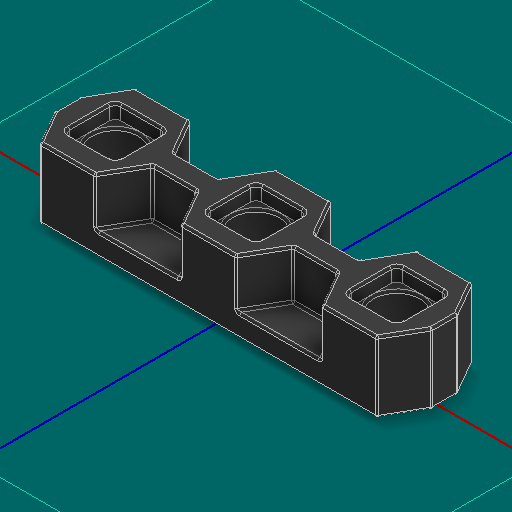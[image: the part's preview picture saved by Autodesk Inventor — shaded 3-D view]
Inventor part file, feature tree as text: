
AUTODESK INVENTOR PART (.ipt)
format: ipt  version: 2025 (Build 290162000, 162)  size: 506,880 bytes
history: native  units: in
note: dims shown in document units (in); Inventor stores cm internally (conversion verified against a paired STEP export)
features: other x3, sketch x1
ambient origin geometry x8: Origin, YZ Plane, XZ Plane, XY Plane, X Axis, Y Axis, Z Axis, Center Point
bodies: Solid1 (feature_tree)
feature tree (4):
  other  "Bearing Flat Low Profile.ipt"
  other  "Solid1::Bearing Flat Low Profile.ipt"
  other  "TaggingFeature1"
  sketch  "Sketch1"  dims[d0=0.3937in]
